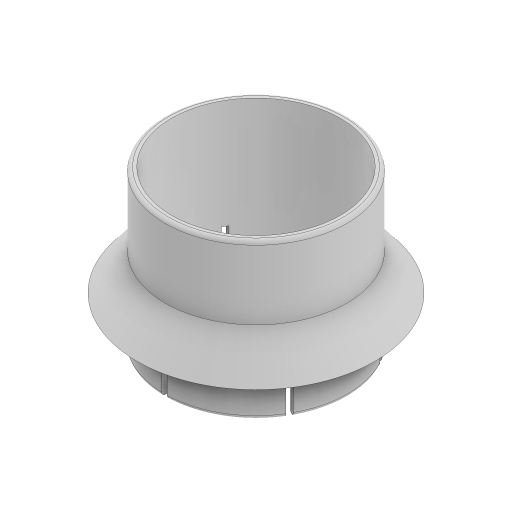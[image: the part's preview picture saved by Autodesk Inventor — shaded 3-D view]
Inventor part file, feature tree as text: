
AUTODESK INVENTOR PART (.ipt)
format: ipt  version: 2023 (Build 270158000, 158)  size: 201,728 bytes
history: native  units: mm
features: sketch x2, revolve x1, extrude x1, pattern_circular x1
ambient origin geometry x8: Origin, YZ Plane, XZ Plane, XY Plane, X Axis, Y Axis, Z Axis, Center Point
bodies: Solid1 (feature_tree)
feature tree (5):
  revolve  "Revolution1"  [1 undecoded]
  extrude  "Extrusion1"  Depth=3.0mm
  pattern_circular  "Circular Pattern1"  [2 undecoded]
  sketch  "Sketch1"  dims[d4=4.0mm d5=25.0mm]
  sketch  "Sketch2"  dims[d7=40.0mm d8=15.0mm d9=50.35mm d10=2.0mm d11=90.0deg d12=20.0mm d13=3.0mm d14=10.0mm d15=25.0mm d16=0.0mm d17=60.0mm d18=360.0deg d20=50.0mm]
note: 3 required parameter values undecoded (feature->parameter linkage not recoverable at this tier; creation-order binding heuristic only, values carry confidence <= 0.55)